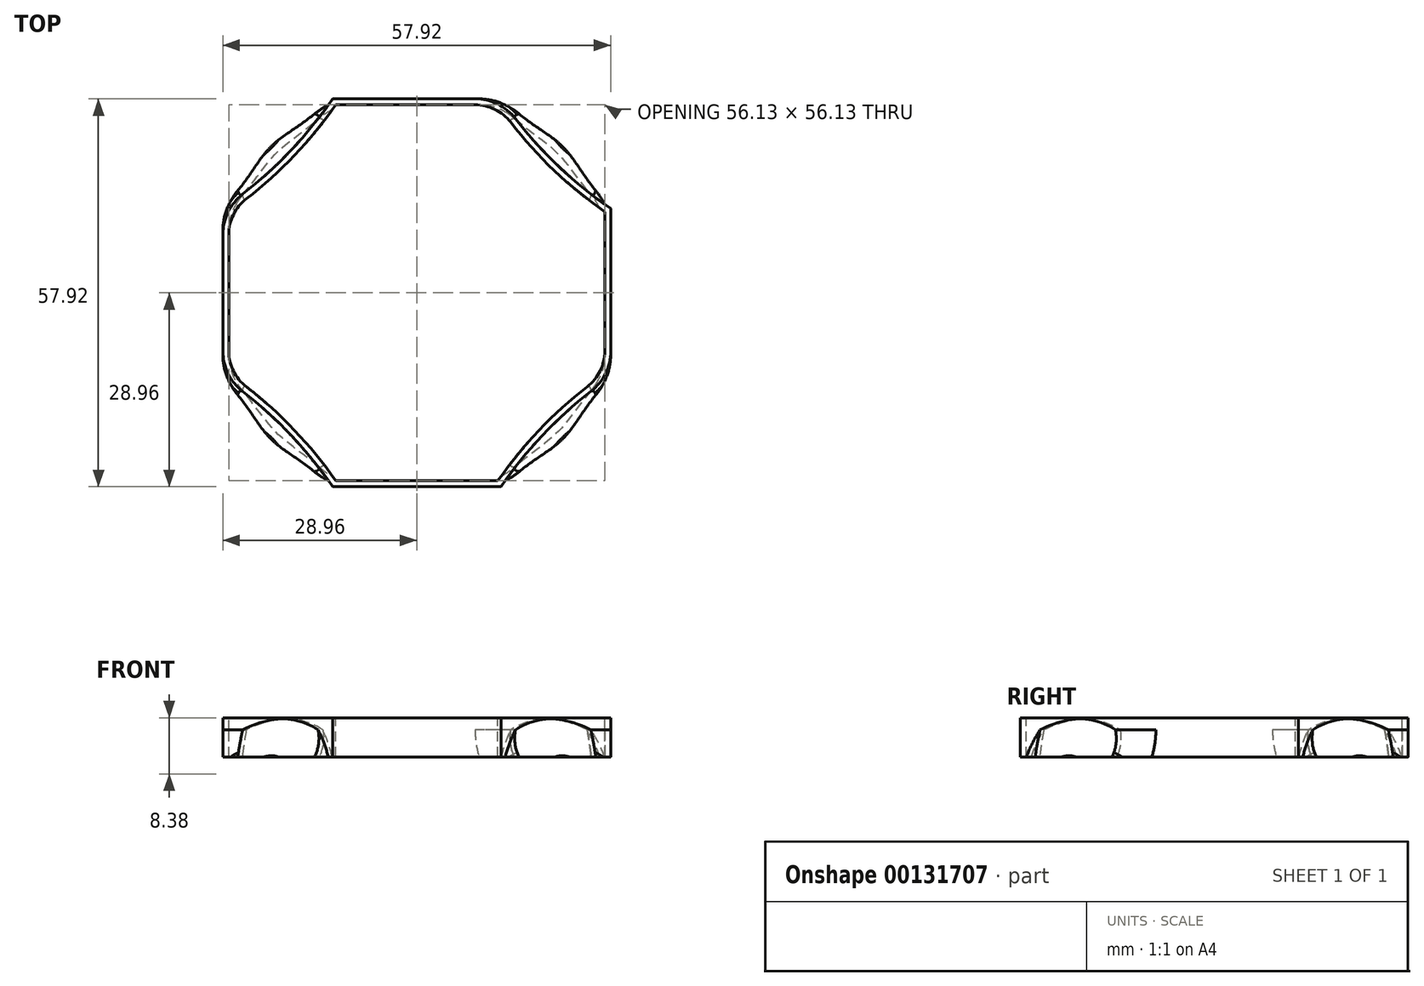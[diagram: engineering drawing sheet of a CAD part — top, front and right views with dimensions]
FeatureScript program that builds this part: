
annotation { "Feature Type Name" : "Feature", "Feature Type Description" : "" }
export const myFeature = defineFeature(function(context is Context, id is Id, definition is map)
    precondition{}
    {
        {
            var Q0;
            Q0=qCreatedBy(makeId("Top.planeOp"),FACE);
            var sketch = newSketch(context, id + "F0", { "sketchPlane" : qUnion([Q0])});
            skLineSegment(sketch, "E0.left", {"start": v(28.96, 12.57) * mm, "end": v(28.96, -12.57) * mm});
            skLineSegment(sketch, "E0.right", {"start": v(-28.96, 12.57) * mm, "end": v(-28.96, -12.57) * mm});
            skPoint(sketch, "E0.middle", {"position": v(0, 0) * mm});
            skLineSegment(sketch, "E1.bottom", {"start": v(12.57, 28.96) * mm, "end": v(-12.57, 28.96) * mm});
            skLineSegment(sketch, "E1.top", {"start": v(12.57, -28.96) * mm, "end": v(-12.57, -28.96) * mm});
            skArc(sketch, "E2", {"start": v(-28.96, 12.57) * mm, "mid": v(-20.01, 20.01) * mm, "end": v(-12.57, 28.96) * mm});
            skArc(sketch, "E3", {"start": v(12.57, 28.96) * mm, "mid": v(20.01, 20.01) * mm, "end": v(28.96, 12.57) * mm});
            skArc(sketch, "E4", {"start": v(28.96, -12.57) * mm, "mid": v(20.01, -20.01) * mm, "end": v(12.57, -28.96) * mm});
            skArc(sketch, "E5", {"start": v(-12.57, -28.96) * mm, "mid": v(-20.01, -20.01) * mm, "end": v(-28.96, -12.57) * mm});
            skSolve(sketch);
        }
        {
            var Q0;
            Q0=qCreatedBy(makeId("Top.planeOp"),FACE);
            cPlane(context, id + "F1", {"entities" : qUnion([Q0]), "cplaneType" : CPlaneType.OFFSET, "offset" : 14.02 * mm, "oppositeDirection" : true, "width" : 152.4 * mm, "height" : 152.4 * mm});
        }
        {
            var Q0;
            Q0=qCreatedBy(id+"F1.planeOp",FACE);
            var sketch = newSketch(context, id + "F2", { "sketchPlane" : qUnion([Q0])});
            skPoint(sketch, "E6.middle", {"position": v(0, 0) * mm});
            skArc(sketch, "E7", {"start": v(-37.14, -19.76) * mm, "mid": v(-28.96, 0) * mm, "end": v(-37.14, 19.76) * mm});
            skArc(sketch, "E8", {"start": v(-19.76, 37.14) * mm, "mid": v(0, 28.96) * mm, "end": v(19.76, 37.14) * mm});
            skArc(sketch, "E9", {"start": v(37.14, 19.76) * mm, "mid": v(28.96, 0) * mm, "end": v(37.14, -19.76) * mm});
            skArc(sketch, "E10", {"start": v(19.76, -37.14) * mm, "mid": v(0, -28.96) * mm, "end": v(-19.76, -37.14) * mm});
            skLineSegment(sketch, "E11", {"start": v(-44.09, 26.7) * mm, "end": v(-37.14, 19.76) * mm});
            skLineSegment(sketch, "E12", {"start": v(-19.76, 37.14) * mm, "end": v(-26.7, 44.09) * mm});
            skLineSegment(sketch, "E13", {"start": v(-26.7, 44.09) * mm, "end": v(-44.09, 26.7) * mm});
            skLineSegment(sketch, "E14", {"start": v(19.76, 37.14) * mm, "end": v(26.7, 44.09) * mm});
            skLineSegment(sketch, "E15", {"start": v(26.7, 44.09) * mm, "end": v(44.09, 26.7) * mm});
            skLineSegment(sketch, "E16", {"start": v(44.09, 26.7) * mm, "end": v(37.14, 19.76) * mm});
            skLineSegment(sketch, "E17", {"start": v(-19.76, -37.14) * mm, "end": v(-26.7, -44.09) * mm});
            skLineSegment(sketch, "E18", {"start": v(-26.7, -44.09) * mm, "end": v(-44.09, -26.7) * mm});
            skLineSegment(sketch, "E19", {"start": v(-44.09, -26.7) * mm, "end": v(-37.14, -19.76) * mm});
            skLineSegment(sketch, "E20", {"start": v(37.14, -19.76) * mm, "end": v(44.09, -26.7) * mm});
            skLineSegment(sketch, "E21", {"start": v(44.09, -26.7) * mm, "end": v(26.7, -44.09) * mm});
            skLineSegment(sketch, "E22", {"start": v(26.7, -44.09) * mm, "end": v(19.76, -37.14) * mm});
            skPoint(sketch, "E23.orphan", {"position": v(-29.11, 29.11) * mm});
            skPoint(sketch, "E24.orphan", {"position": v(29.1, 29.1) * mm});
            skPoint(sketch, "E25.orphan", {"position": v(29.11, -29.11) * mm});
            skPoint(sketch, "E26.orphan", {"position": v(-29.1, -29.1) * mm});
            skLineSegment(sketch, "E27.bottom", {"start": v(54.62, -53.7) * mm, "end": v(-54.62, -53.7) * mm});
            skLineSegment(sketch, "E27.top", {"start": v(54.62, 53.7) * mm, "end": v(-54.62, 53.7) * mm});
            skLineSegment(sketch, "E27.left", {"start": v(54.62, -53.7) * mm, "end": v(54.62, 53.7) * mm});
            skLineSegment(sketch, "E27.right", {"start": v(-54.62, -53.7) * mm, "end": v(-54.62, 53.7) * mm});
            skSolve(sketch);
        }
        {
            var Q0;
            Q0=makeQuery(id+"F0.imprint","IMPRINT",FACE,{"disambiguationData":[TD([[makeQuery(id+"F0.imprint","IMPRINT",EDGE,{"derivedFrom":sQuery(id+"F0.wireOp",EDGE,"E0.left")}),-1.0]])]});
            var Q1;
            Q1=qCreatedBy(id+"F1.planeOp",FACE);
            extrude(context, id + "F3", {"entities" : qUnion([Q0]), "endBound" : BoundingType.UP_TO_SURFACE, "oppositeDirection" : true, "endBoundEntityFace" : qUnion([Q1]), "depth" : 25.4 * mm});
        }
        {
            var Q0;
            Q0=makeQuery(id+"F0.imprint","IMPRINT",FACE,{"disambiguationData":[TD([[makeQuery(id+"F0.imprint","IMPRINT",EDGE,{"derivedFrom":sQuery(id+"F0.wireOp",EDGE,"E0.left")}),-1.0]])]});
            extrude(context, id + "F4", {"entities" : qUnion([Q0]), "operationType" : NewBodyOperationType.ADD, "depth" : 25.4 * mm});
        }
        {
            var Q0;
            Q0=qCreatedBy(id+"F1.planeOp",FACE);
            var sketch = newSketch(context, id + "F5", { "sketchPlane" : qUnion([Q0])});
            skLineSegment(sketch, "E28", {"start": v(-26.36, -26.36) * mm, "end": v(26.36, 26.36) * mm});
            skLineSegment(sketch, "E29", {"start": v(26.36, -26.36) * mm, "end": v(-26.36, 26.36) * mm});
            skSolve(sketch);
        }
        {
            var Q0;
            Q0=qCreatedBy(makeId("Front.planeOp"),FACE);
            var Q1;
            Q1=sQuery(id+"F5.wireOp",EDGE,"E28");
            cPlane(context, id + "F6", {"entities" : qUnion([Q0, Q1]), "cplaneType" : CPlaneType.LINE_ANGLE, "offset" : 25.4 * mm, "angle" : 0 * degree, "width" : 152.4 * mm, "height" : 152.4 * mm});
        }
        {
            var Q0;
            Q0=qCreatedBy(makeId("Front.planeOp"),FACE);
            var Q1;
            Q1=sQuery(id+"F5.wireOp",EDGE,"E29");
            cPlane(context, id + "F7", {"entities" : qUnion([Q0, Q1]), "cplaneType" : CPlaneType.LINE_ANGLE, "offset" : 25.4 * mm, "angle" : 0 * degree, "width" : 152.4 * mm, "height" : 152.4 * mm});
        }
        {
            var Q0;
            Q0=qCreatedBy(id+"F6.planeOp",FACE);
            var sketch = newSketch(context, id + "F8", { "sketchPlane" : qUnion([Q0])});
            skCircle(sketch, "E30", {"center": v(50.22, 20.65) * mm, "radius": 28.32 * mm});
            skLineSegment(sketch, "E31.bottom", {"start": v(50.22, 20.65) * mm, "end": v(12.75, 20.65) * mm});
            skLineSegment(sketch, "E31.top", {"start": v(50.22, -14.02) * mm, "end": v(12.75, -14.02) * mm});
            skLineSegment(sketch, "E31.left", {"start": v(50.22, 20.65) * mm, "end": v(50.22, -14.02) * mm});
            skLineSegment(sketch, "E31.right", {"start": v(12.75, 20.65) * mm, "end": v(12.75, -14.02) * mm});
            skCircle(sketch, "E32", {"center": v(-50.22, 20.65) * mm, "radius": 28.32 * mm});
            skLineSegment(sketch, "E33.bottom", {"start": v(-50.22, 20.65) * mm, "end": v(-12.75, 20.65) * mm});
            skLineSegment(sketch, "E33.top", {"start": v(-50.22, -14.02) * mm, "end": v(-12.75, -14.02) * mm});
            skLineSegment(sketch, "E33.left", {"start": v(-50.22, 20.65) * mm, "end": v(-50.22, -14.02) * mm});
            skLineSegment(sketch, "E33.right", {"start": v(-12.75, 20.65) * mm, "end": v(-12.75, -14.02) * mm});
            skSolve(sketch);
        }
        {
            var Q0;
            Q0=qCreatedBy(id+"F7.planeOp",FACE);
            var sketch = newSketch(context, id + "F9", { "sketchPlane" : qUnion([Q0])});
            skCircle(sketch, "E34", {"center": v(-50.22, 20.65) * mm, "radius": 28.32 * mm});
            skCircle(sketch, "E35", {"center": v(50.22, 20.65) * mm, "radius": 28.32 * mm});
            skLineSegment(sketch, "E36.bottom", {"start": v(-50.22, 20.65) * mm, "end": v(-12.75, 20.65) * mm});
            skLineSegment(sketch, "E36.top", {"start": v(-50.22, -14.02) * mm, "end": v(-12.75, -14.02) * mm});
            skLineSegment(sketch, "E36.left", {"start": v(-50.22, 20.65) * mm, "end": v(-50.22, -14.02) * mm});
            skLineSegment(sketch, "E36.right", {"start": v(-12.75, 20.65) * mm, "end": v(-12.75, -14.02) * mm});
            skLineSegment(sketch, "E37.bottom", {"start": v(50.22, 20.65) * mm, "end": v(12.75, 20.65) * mm});
            skLineSegment(sketch, "E37.top", {"start": v(50.22, -14.02) * mm, "end": v(12.75, -14.02) * mm});
            skLineSegment(sketch, "E37.left", {"start": v(50.22, 20.65) * mm, "end": v(50.22, -14.02) * mm});
            skLineSegment(sketch, "E37.right", {"start": v(12.75, 20.65) * mm, "end": v(12.75, -14.02) * mm});
            skSolve(sketch);
        }
        {
            var Q0;
            {var subQ1=sQuery(id+"F8.wireOp",EDGE,"E31.top");Q0=makeQuery(id+"F8.imprint","IMPRINT",FACE,{"disambiguationData":[TD([[makeQuery(id+"F8.imprint","IMPRINT",EDGE,{"derivedFrom":subQ1}),-1.0]])]});}
            var Q1;
            {var subQ1=sQuery(id+"F8.wireOp",EDGE,"E33.top");Q1=makeQuery(id+"F8.imprint","IMPRINT",FACE,{"disambiguationData":[TD([[makeQuery(id+"F8.imprint","IMPRINT",EDGE,{"derivedFrom":subQ1}),1.0]])]});}
            extrude(context, id + "F10", {"entities" : qUnion([Q0, Q1]), "operationType" : NewBodyOperationType.ADD, "endBound" : BoundingType.SYMMETRIC, "depth" : 38.1 * mm});
        }
        {
            var Q0;
            {var subQ1=sQuery(id+"F9.wireOp",EDGE,"E36.top");Q0=makeQuery(id+"F9.imprint","IMPRINT",FACE,{"disambiguationData":[TD([[makeQuery(id+"F9.imprint","IMPRINT",EDGE,{"derivedFrom":subQ1}),1.0]])]});}
            var Q1;
            {var subQ1=sQuery(id+"F9.wireOp",EDGE,"E37.top");Q1=makeQuery(id+"F9.imprint","IMPRINT",FACE,{"disambiguationData":[TD([[makeQuery(id+"F9.imprint","IMPRINT",EDGE,{"derivedFrom":subQ1}),-1.0]])]});}
            extrude(context, id + "F11", {"entities" : qUnion([Q0, Q1]), "operationType" : NewBodyOperationType.ADD, "endBound" : BoundingType.SYMMETRIC, "depth" : 38.1 * mm});
        }
        {
            var Q0;
            Q0=makeQuery(id+"F10.opExtrude","CAP_EDGE",EDGE,{"disambiguationData":[OSD([sQuery(id+"F8.wireOp",EDGE,"E30")])],"isStart":false});
            var Q1;
            Q1=makeQuery(id+"F10.opExtrude","CAP_EDGE",EDGE,{"disambiguationData":[OSD([sQuery(id+"F8.wireOp",EDGE,"E30")])],"isStart":true});
            var Q2;
            Q2=makeQuery(id+"F10.opExtrude","CAP_EDGE",EDGE,{"disambiguationData":[OSD([sQuery(id+"F8.wireOp",EDGE,"E32")])],"isStart":false});
            var Q3;
            Q3=makeQuery(id+"F10.opExtrude","CAP_EDGE",EDGE,{"disambiguationData":[OSD([sQuery(id+"F8.wireOp",EDGE,"E32")])],"isStart":true});
            var Q4;
            Q4=makeQuery(id+"F11.opExtrude","CAP_EDGE",EDGE,{"disambiguationData":[OSD([sQuery(id+"F9.wireOp",EDGE,"E35")])],"isStart":true});
            var Q5;
            Q5=makeQuery(id+"F11.opExtrude","CAP_EDGE",EDGE,{"disambiguationData":[OSD([sQuery(id+"F9.wireOp",EDGE,"E35")])],"isStart":false});
            var Q6;
            Q6=makeQuery(id+"F11.opExtrude","CAP_EDGE",EDGE,{"disambiguationData":[OSD([sQuery(id+"F9.wireOp",EDGE,"E34")])],"isStart":true});
            var Q7;
            Q7=makeQuery(id+"F11.opExtrude","CAP_EDGE",EDGE,{"disambiguationData":[OSD([sQuery(id+"F9.wireOp",EDGE,"E34")])],"isStart":false});
            fillet(context, id + "F12", {"entities" : qUnion([Q0, Q1, Q2, Q3, Q4, Q5, Q6, Q7]), "radius" : 19.05 * mm, "tangentPropagation" : true, "allowEdgeOverflow" : false});
        }
        {
            var Q0;
            Q0=makeQuery(id+"F2.imprint","IMPRINT",FACE,{"disambiguationData":[TD([[makeQuery(id+"F2.imprint","IMPRINT",EDGE,{"derivedFrom":sQuery(id+"F2.wireOp",EDGE,"E7")}),1.0]])]});
            extrude(context, id + "F13", {"entities" : qUnion([Q0]), "operationType" : NewBodyOperationType.REMOVE, "depth" : 50.8 * mm});
        }
        {
            var Q0;
            Q0=makeQuery(id+"F13.boolean.opBoolean","INTERSECT",EDGE,{"derivedFrom":[makeQuery(id+"F12.opFillet","BLEND_FACE",FACE,{"disambiguationData":[OSD([sQuery(id+"F8.wireOp",EDGE,"E30")])]}),makeQuery(id+"F13.opExtrude","SWEPT_FACE",FACE,{"disambiguationData":[OSD([sQuery(id+"F2.wireOp",EDGE,"E19")])]})]});
            var Q1;
            Q1=makeQuery(id+"F13.boolean.opBoolean","INTERSECT",EDGE,{"derivedFrom":[makeQuery(id+"F12.opFillet","BLEND_FACE",FACE,{"disambiguationData":[OSD([sQuery(id+"F8.wireOp",EDGE,"E30")])]}),makeQuery(id+"F13.opExtrude","SWEPT_FACE",FACE,{"disambiguationData":[OSD([sQuery(id+"F2.wireOp",EDGE,"E17")])]})]});
            var Q2;
            Q2=makeQuery(id+"F13.boolean.opBoolean","INTERSECT",EDGE,{"derivedFrom":[makeQuery(id+"F12.opFillet","BLEND_FACE",FACE,{"disambiguationData":[OSD([sQuery(id+"F8.wireOp",EDGE,"E32")])]}),makeQuery(id+"F13.opExtrude","SWEPT_FACE",FACE,{"disambiguationData":[OSD([sQuery(id+"F2.wireOp",EDGE,"E14")])]})]});
            var Q3;
            Q3=makeQuery(id+"F13.boolean.opBoolean","INTERSECT",EDGE,{"derivedFrom":[makeQuery(id+"F12.opFillet","BLEND_FACE",FACE,{"disambiguationData":[OSD([sQuery(id+"F8.wireOp",EDGE,"E32")])]}),makeQuery(id+"F13.opExtrude","SWEPT_FACE",FACE,{"disambiguationData":[OSD([sQuery(id+"F2.wireOp",EDGE,"E16")])]})]});
            var Q4;
            Q4=makeQuery(id+"F13.boolean.opBoolean","INTERSECT",EDGE,{"derivedFrom":[makeQuery(id+"F12.opFillet","BLEND_FACE",FACE,{"disambiguationData":[OSD([sQuery(id+"F9.wireOp",EDGE,"E35")])]}),makeQuery(id+"F13.opExtrude","SWEPT_FACE",FACE,{"disambiguationData":[OSD([sQuery(id+"F2.wireOp",EDGE,"E11")])]})]});
            var Q5;
            Q5=makeQuery(id+"F13.boolean.opBoolean","INTERSECT",EDGE,{"derivedFrom":[makeQuery(id+"F12.opFillet","BLEND_FACE",FACE,{"disambiguationData":[OSD([sQuery(id+"F9.wireOp",EDGE,"E35")])]}),makeQuery(id+"F13.opExtrude","SWEPT_FACE",FACE,{"disambiguationData":[OSD([sQuery(id+"F2.wireOp",EDGE,"E12")])]})]});
            var Q6;
            Q6=makeQuery(id+"F13.boolean.opBoolean","INTERSECT",EDGE,{"derivedFrom":[makeQuery(id+"F12.opFillet","BLEND_FACE",FACE,{"disambiguationData":[OSD([sQuery(id+"F9.wireOp",EDGE,"E34")])]}),makeQuery(id+"F13.opExtrude","SWEPT_FACE",FACE,{"disambiguationData":[OSD([sQuery(id+"F2.wireOp",EDGE,"E22")])]})]});
            var Q7;
            Q7=makeQuery(id+"F13.boolean.opBoolean","INTERSECT",EDGE,{"derivedFrom":[makeQuery(id+"F12.opFillet","BLEND_FACE",FACE,{"disambiguationData":[OSD([sQuery(id+"F9.wireOp",EDGE,"E34")])]}),makeQuery(id+"F13.opExtrude","SWEPT_FACE",FACE,{"disambiguationData":[OSD([sQuery(id+"F2.wireOp",EDGE,"E20")])]})]});
            fillet(context, id + "F14", {"entities" : qUnion([Q0, Q1, Q2, Q3, Q4, Q5, Q6, Q7]), "radius" : 5.6 * mm, "tangentPropagation" : true, "allowEdgeOverflow" : false});
        }
        {
            var Q0;
            {var subQ0=sQuery(id+"F0.wireOp",EDGE,"E5");Q0=makeQuery(id+"F12.opFillet","BLEND_EDGE",EDGE,{"blendedFrom":[makeQuery(id+"F10.opExtrude","CAP_EDGE",EDGE,{"disambiguationData":[OSD([sQuery(id+"F8.wireOp",EDGE,"E30")])],"isStart":false}),makeQuery(id+"F4.boolean.opBoolean","MERGE",FACE,{"derivedFrom":[makeQuery(id+"F3.opExtrude","SWEPT_FACE",FACE,{"disambiguationData":[OSD([subQ0])]}),makeQuery(id+"F4.opExtrude","SWEPT_FACE",FACE,{"disambiguationData":[OSD([subQ0])]})]})],"blendedInto":[makeQuery(id+"F4.boolean.opBoolean","MERGE",FACE,{"derivedFrom":[makeQuery(id+"F3.opExtrude","SWEPT_FACE",FACE,{"disambiguationData":[OSD([subQ0])]}),makeQuery(id+"F4.opExtrude","SWEPT_FACE",FACE,{"disambiguationData":[OSD([subQ0])]})]})]});}
            var Q1;
            {var subQ0=sQuery(id+"F0.wireOp",EDGE,"E0.right");Q1=makeQuery(id+"F12.opFillet","BLEND_EDGE",EDGE,{"blendedFrom":[makeQuery(id+"F10.opExtrude","CAP_EDGE",EDGE,{"disambiguationData":[OSD([sQuery(id+"F8.wireOp",EDGE,"E30")])],"isStart":false}),makeQuery(id+"F4.boolean.opBoolean","MERGE",FACE,{"derivedFrom":[makeQuery(id+"F3.opExtrude","SWEPT_FACE",FACE,{"disambiguationData":[OSD([subQ0])]}),makeQuery(id+"F4.opExtrude","SWEPT_FACE",FACE,{"disambiguationData":[OSD([subQ0])]})]})],"blendedInto":[makeQuery(id+"F4.boolean.opBoolean","MERGE",FACE,{"derivedFrom":[makeQuery(id+"F3.opExtrude","SWEPT_FACE",FACE,{"disambiguationData":[OSD([subQ0])]}),makeQuery(id+"F4.opExtrude","SWEPT_FACE",FACE,{"disambiguationData":[OSD([subQ0])]})]})]});}
            var Q2;
            {var subQ0=sQuery(id+"F0.wireOp",EDGE,"E1.top");Q2=makeQuery(id+"F12.opFillet","BLEND_EDGE",EDGE,{"blendedFrom":[makeQuery(id+"F10.opExtrude","CAP_EDGE",EDGE,{"disambiguationData":[OSD([sQuery(id+"F8.wireOp",EDGE,"E30")])],"isStart":true}),makeQuery(id+"F4.boolean.opBoolean","MERGE",FACE,{"derivedFrom":[makeQuery(id+"F3.opExtrude","SWEPT_FACE",FACE,{"disambiguationData":[OSD([subQ0])]}),makeQuery(id+"F4.opExtrude","SWEPT_FACE",FACE,{"disambiguationData":[OSD([subQ0])]})]})],"blendedInto":[makeQuery(id+"F4.boolean.opBoolean","MERGE",FACE,{"derivedFrom":[makeQuery(id+"F3.opExtrude","SWEPT_FACE",FACE,{"disambiguationData":[OSD([subQ0])]}),makeQuery(id+"F4.opExtrude","SWEPT_FACE",FACE,{"disambiguationData":[OSD([subQ0])]})]})]});}
            var Q3;
            {var subQ0=sQuery(id+"F0.wireOp",EDGE,"E1.bottom");Q3=makeQuery(id+"F12.opFillet","BLEND_EDGE",EDGE,{"blendedFrom":[makeQuery(id+"F10.opExtrude","CAP_EDGE",EDGE,{"disambiguationData":[OSD([sQuery(id+"F8.wireOp",EDGE,"E32")])],"isStart":false}),makeQuery(id+"F4.boolean.opBoolean","MERGE",FACE,{"derivedFrom":[makeQuery(id+"F3.opExtrude","SWEPT_FACE",FACE,{"disambiguationData":[OSD([subQ0])]}),makeQuery(id+"F4.opExtrude","SWEPT_FACE",FACE,{"disambiguationData":[OSD([subQ0])]})]})],"blendedInto":[makeQuery(id+"F4.boolean.opBoolean","MERGE",FACE,{"derivedFrom":[makeQuery(id+"F3.opExtrude","SWEPT_FACE",FACE,{"disambiguationData":[OSD([subQ0])]}),makeQuery(id+"F4.opExtrude","SWEPT_FACE",FACE,{"disambiguationData":[OSD([subQ0])]})]})]});}
            var Q4;
            {var subQ0=sQuery(id+"F0.wireOp",EDGE,"E3");Q4=makeQuery(id+"F12.opFillet","BLEND_EDGE",EDGE,{"blendedFrom":[makeQuery(id+"F10.opExtrude","CAP_EDGE",EDGE,{"disambiguationData":[OSD([sQuery(id+"F8.wireOp",EDGE,"E32")])],"isStart":false}),makeQuery(id+"F4.boolean.opBoolean","MERGE",FACE,{"derivedFrom":[makeQuery(id+"F3.opExtrude","SWEPT_FACE",FACE,{"disambiguationData":[OSD([subQ0])]}),makeQuery(id+"F4.opExtrude","SWEPT_FACE",FACE,{"disambiguationData":[OSD([subQ0])]})]})],"blendedInto":[makeQuery(id+"F4.boolean.opBoolean","MERGE",FACE,{"derivedFrom":[makeQuery(id+"F3.opExtrude","SWEPT_FACE",FACE,{"disambiguationData":[OSD([subQ0])]}),makeQuery(id+"F4.opExtrude","SWEPT_FACE",FACE,{"disambiguationData":[OSD([subQ0])]})]})]});}
            var Q5;
            {var subQ0=sQuery(id+"F0.wireOp",EDGE,"E0.left");Q5=makeQuery(id+"F12.opFillet","BLEND_EDGE",EDGE,{"blendedFrom":[makeQuery(id+"F10.opExtrude","CAP_EDGE",EDGE,{"disambiguationData":[OSD([sQuery(id+"F8.wireOp",EDGE,"E32")])],"isStart":true}),makeQuery(id+"F4.boolean.opBoolean","MERGE",FACE,{"derivedFrom":[makeQuery(id+"F3.opExtrude","SWEPT_FACE",FACE,{"disambiguationData":[OSD([subQ0])]}),makeQuery(id+"F4.opExtrude","SWEPT_FACE",FACE,{"disambiguationData":[OSD([subQ0])]})]})],"blendedInto":[makeQuery(id+"F4.boolean.opBoolean","MERGE",FACE,{"derivedFrom":[makeQuery(id+"F3.opExtrude","SWEPT_FACE",FACE,{"disambiguationData":[OSD([subQ0])]}),makeQuery(id+"F4.opExtrude","SWEPT_FACE",FACE,{"disambiguationData":[OSD([subQ0])]})]})]});}
            var Q6;
            {var subQ0=sQuery(id+"F0.wireOp",EDGE,"E0.right");Q6=makeQuery(id+"F12.opFillet","BLEND_EDGE",EDGE,{"blendedFrom":[makeQuery(id+"F11.opExtrude","CAP_EDGE",EDGE,{"disambiguationData":[OSD([sQuery(id+"F9.wireOp",EDGE,"E35")])],"isStart":true}),makeQuery(id+"F4.boolean.opBoolean","MERGE",FACE,{"derivedFrom":[makeQuery(id+"F3.opExtrude","SWEPT_FACE",FACE,{"disambiguationData":[OSD([subQ0])]}),makeQuery(id+"F4.opExtrude","SWEPT_FACE",FACE,{"disambiguationData":[OSD([subQ0])]})]})],"blendedInto":[makeQuery(id+"F4.boolean.opBoolean","MERGE",FACE,{"derivedFrom":[makeQuery(id+"F3.opExtrude","SWEPT_FACE",FACE,{"disambiguationData":[OSD([subQ0])]}),makeQuery(id+"F4.opExtrude","SWEPT_FACE",FACE,{"disambiguationData":[OSD([subQ0])]})]})]});}
            var Q7;
            {var subQ0=sQuery(id+"F0.wireOp",EDGE,"E2");Q7=makeQuery(id+"F12.opFillet","BLEND_EDGE",EDGE,{"blendedFrom":[makeQuery(id+"F11.opExtrude","CAP_EDGE",EDGE,{"disambiguationData":[OSD([sQuery(id+"F9.wireOp",EDGE,"E35")])],"isStart":true}),makeQuery(id+"F4.boolean.opBoolean","MERGE",FACE,{"derivedFrom":[makeQuery(id+"F3.opExtrude","SWEPT_FACE",FACE,{"disambiguationData":[OSD([subQ0])]}),makeQuery(id+"F4.opExtrude","SWEPT_FACE",FACE,{"disambiguationData":[OSD([subQ0])]})]})],"blendedInto":[makeQuery(id+"F4.boolean.opBoolean","MERGE",FACE,{"derivedFrom":[makeQuery(id+"F3.opExtrude","SWEPT_FACE",FACE,{"disambiguationData":[OSD([subQ0])]}),makeQuery(id+"F4.opExtrude","SWEPT_FACE",FACE,{"disambiguationData":[OSD([subQ0])]})]})]});}
            var Q8;
            {var subQ0=sQuery(id+"F0.wireOp",EDGE,"E1.bottom");Q8=makeQuery(id+"F12.opFillet","BLEND_EDGE",EDGE,{"blendedFrom":[makeQuery(id+"F11.opExtrude","CAP_EDGE",EDGE,{"disambiguationData":[OSD([sQuery(id+"F9.wireOp",EDGE,"E35")])],"isStart":false}),makeQuery(id+"F4.boolean.opBoolean","MERGE",FACE,{"derivedFrom":[makeQuery(id+"F3.opExtrude","SWEPT_FACE",FACE,{"disambiguationData":[OSD([subQ0])]}),makeQuery(id+"F4.opExtrude","SWEPT_FACE",FACE,{"disambiguationData":[OSD([subQ0])]})]})],"blendedInto":[makeQuery(id+"F4.boolean.opBoolean","MERGE",FACE,{"derivedFrom":[makeQuery(id+"F3.opExtrude","SWEPT_FACE",FACE,{"disambiguationData":[OSD([subQ0])]}),makeQuery(id+"F4.opExtrude","SWEPT_FACE",FACE,{"disambiguationData":[OSD([subQ0])]})]})]});}
            var Q9;
            {var subQ0=sQuery(id+"F0.wireOp",EDGE,"E0.left");Q9=makeQuery(id+"F12.opFillet","BLEND_EDGE",EDGE,{"blendedFrom":[makeQuery(id+"F11.opExtrude","CAP_EDGE",EDGE,{"disambiguationData":[OSD([sQuery(id+"F9.wireOp",EDGE,"E34")])],"isStart":false}),makeQuery(id+"F4.boolean.opBoolean","MERGE",FACE,{"derivedFrom":[makeQuery(id+"F3.opExtrude","SWEPT_FACE",FACE,{"disambiguationData":[OSD([subQ0])]}),makeQuery(id+"F4.opExtrude","SWEPT_FACE",FACE,{"disambiguationData":[OSD([subQ0])]})]})],"blendedInto":[makeQuery(id+"F4.boolean.opBoolean","MERGE",FACE,{"derivedFrom":[makeQuery(id+"F3.opExtrude","SWEPT_FACE",FACE,{"disambiguationData":[OSD([subQ0])]}),makeQuery(id+"F4.opExtrude","SWEPT_FACE",FACE,{"disambiguationData":[OSD([subQ0])]})]})]});}
            var Q10;
            {var subQ0=sQuery(id+"F0.wireOp",EDGE,"E4");Q10=makeQuery(id+"F12.opFillet","BLEND_EDGE",EDGE,{"blendedFrom":[makeQuery(id+"F11.opExtrude","CAP_EDGE",EDGE,{"disambiguationData":[OSD([sQuery(id+"F9.wireOp",EDGE,"E34")])],"isStart":false}),makeQuery(id+"F4.boolean.opBoolean","MERGE",FACE,{"derivedFrom":[makeQuery(id+"F3.opExtrude","SWEPT_FACE",FACE,{"disambiguationData":[OSD([subQ0])]}),makeQuery(id+"F4.opExtrude","SWEPT_FACE",FACE,{"disambiguationData":[OSD([subQ0])]})]})],"blendedInto":[makeQuery(id+"F4.boolean.opBoolean","MERGE",FACE,{"derivedFrom":[makeQuery(id+"F3.opExtrude","SWEPT_FACE",FACE,{"disambiguationData":[OSD([subQ0])]}),makeQuery(id+"F4.opExtrude","SWEPT_FACE",FACE,{"disambiguationData":[OSD([subQ0])]})]})]});}
            var Q11;
            {var subQ0=sQuery(id+"F0.wireOp",EDGE,"E1.top");Q11=makeQuery(id+"F12.opFillet","BLEND_EDGE",EDGE,{"blendedFrom":[makeQuery(id+"F11.opExtrude","CAP_EDGE",EDGE,{"disambiguationData":[OSD([sQuery(id+"F9.wireOp",EDGE,"E34")])],"isStart":true}),makeQuery(id+"F4.boolean.opBoolean","MERGE",FACE,{"derivedFrom":[makeQuery(id+"F3.opExtrude","SWEPT_FACE",FACE,{"disambiguationData":[OSD([subQ0])]}),makeQuery(id+"F4.opExtrude","SWEPT_FACE",FACE,{"disambiguationData":[OSD([subQ0])]})]})],"blendedInto":[makeQuery(id+"F4.boolean.opBoolean","MERGE",FACE,{"derivedFrom":[makeQuery(id+"F3.opExtrude","SWEPT_FACE",FACE,{"disambiguationData":[OSD([subQ0])]}),makeQuery(id+"F4.opExtrude","SWEPT_FACE",FACE,{"disambiguationData":[OSD([subQ0])]})]})]});}
            fillet(context, id + "F15", {"entities" : qUnion([Q0, Q1, Q2, Q3, Q4, Q5, Q6, Q7, Q8, Q9, Q10, Q11]), "radius" : 7.62 * mm, "tangentPropagation" : true, "allowEdgeOverflow" : false});
        }
        {
            var Q0;
            {var subQ0=sQuery(id+"F0.wireOp",EDGE,"E0.right");var subQ1=makeQuery(id+"F10.opExtrude","CAP_EDGE",EDGE,{"disambiguationData":[OSD([sQuery(id+"F8.wireOp",EDGE,"E30")])],"isStart":false});var subQ2=sQuery(id+"F0.wireOp",EDGE,"E5");Q0=makeQuery(id+"F15.opFillet","BLEND_EDGE",EDGE,{"blendedFrom":[makeQuery(id+"F12.opFillet","BLEND_EDGE",EDGE,{"blendedFrom":[subQ1,makeQuery(id+"F4.boolean.opBoolean","MERGE",FACE,{"derivedFrom":[makeQuery(id+"F3.opExtrude","SWEPT_FACE",FACE,{"disambiguationData":[OSD([subQ2])]}),makeQuery(id+"F4.opExtrude","SWEPT_FACE",FACE,{"disambiguationData":[OSD([subQ2])]})]})],"blendedInto":[makeQuery(id+"F4.boolean.opBoolean","MERGE",FACE,{"derivedFrom":[makeQuery(id+"F3.opExtrude","SWEPT_FACE",FACE,{"disambiguationData":[OSD([subQ2])]}),makeQuery(id+"F4.opExtrude","SWEPT_FACE",FACE,{"disambiguationData":[OSD([subQ2])]})]})]}),makeQuery(id+"F12.opFillet","BLEND_EDGE",EDGE,{"blendedFrom":[subQ1,makeQuery(id+"F4.boolean.opBoolean","MERGE",FACE,{"derivedFrom":[makeQuery(id+"F3.opExtrude","SWEPT_FACE",FACE,{"disambiguationData":[OSD([subQ0])]}),makeQuery(id+"F4.opExtrude","SWEPT_FACE",FACE,{"disambiguationData":[OSD([subQ0])]})]})],"blendedInto":[makeQuery(id+"F4.boolean.opBoolean","MERGE",FACE,{"derivedFrom":[makeQuery(id+"F3.opExtrude","SWEPT_FACE",FACE,{"disambiguationData":[OSD([subQ0])]}),makeQuery(id+"F4.opExtrude","SWEPT_FACE",FACE,{"disambiguationData":[OSD([subQ0])]})]})]})],"blendedInto":[]});}
            var Q1;
            {var subQ0=sQuery(id+"F0.wireOp",EDGE,"E1.top");var subQ1=makeQuery(id+"F10.opExtrude","CAP_EDGE",EDGE,{"disambiguationData":[OSD([sQuery(id+"F8.wireOp",EDGE,"E30")])],"isStart":true});var subQ2=sQuery(id+"F0.wireOp",EDGE,"E5");Q1=makeQuery(id+"F15.opFillet","BLEND_EDGE",EDGE,{"blendedFrom":[makeQuery(id+"F12.opFillet","BLEND_EDGE",EDGE,{"blendedFrom":[subQ1,makeQuery(id+"F4.boolean.opBoolean","MERGE",FACE,{"derivedFrom":[makeQuery(id+"F3.opExtrude","SWEPT_FACE",FACE,{"disambiguationData":[OSD([subQ2])]}),makeQuery(id+"F4.opExtrude","SWEPT_FACE",FACE,{"disambiguationData":[OSD([subQ2])]})]})],"blendedInto":[makeQuery(id+"F4.boolean.opBoolean","MERGE",FACE,{"derivedFrom":[makeQuery(id+"F3.opExtrude","SWEPT_FACE",FACE,{"disambiguationData":[OSD([subQ2])]}),makeQuery(id+"F4.opExtrude","SWEPT_FACE",FACE,{"disambiguationData":[OSD([subQ2])]})]})]}),makeQuery(id+"F12.opFillet","BLEND_EDGE",EDGE,{"blendedFrom":[subQ1,makeQuery(id+"F4.boolean.opBoolean","MERGE",FACE,{"derivedFrom":[makeQuery(id+"F3.opExtrude","SWEPT_FACE",FACE,{"disambiguationData":[OSD([subQ0])]}),makeQuery(id+"F4.opExtrude","SWEPT_FACE",FACE,{"disambiguationData":[OSD([subQ0])]})]})],"blendedInto":[makeQuery(id+"F4.boolean.opBoolean","MERGE",FACE,{"derivedFrom":[makeQuery(id+"F3.opExtrude","SWEPT_FACE",FACE,{"disambiguationData":[OSD([subQ0])]}),makeQuery(id+"F4.opExtrude","SWEPT_FACE",FACE,{"disambiguationData":[OSD([subQ0])]})]})]})],"blendedInto":[]});}
            var Q2;
            {var subQ0=sQuery(id+"F0.wireOp",EDGE,"E1.bottom");var subQ1=makeQuery(id+"F10.opExtrude","CAP_EDGE",EDGE,{"disambiguationData":[OSD([sQuery(id+"F8.wireOp",EDGE,"E32")])],"isStart":false});var subQ2=sQuery(id+"F0.wireOp",EDGE,"E3");Q2=makeQuery(id+"F15.opFillet","BLEND_EDGE",EDGE,{"blendedFrom":[makeQuery(id+"F12.opFillet","BLEND_EDGE",EDGE,{"blendedFrom":[subQ1,makeQuery(id+"F4.boolean.opBoolean","MERGE",FACE,{"derivedFrom":[makeQuery(id+"F3.opExtrude","SWEPT_FACE",FACE,{"disambiguationData":[OSD([subQ2])]}),makeQuery(id+"F4.opExtrude","SWEPT_FACE",FACE,{"disambiguationData":[OSD([subQ2])]})]})],"blendedInto":[makeQuery(id+"F4.boolean.opBoolean","MERGE",FACE,{"derivedFrom":[makeQuery(id+"F3.opExtrude","SWEPT_FACE",FACE,{"disambiguationData":[OSD([subQ2])]}),makeQuery(id+"F4.opExtrude","SWEPT_FACE",FACE,{"disambiguationData":[OSD([subQ2])]})]})]}),makeQuery(id+"F12.opFillet","BLEND_EDGE",EDGE,{"blendedFrom":[subQ1,makeQuery(id+"F4.boolean.opBoolean","MERGE",FACE,{"derivedFrom":[makeQuery(id+"F3.opExtrude","SWEPT_FACE",FACE,{"disambiguationData":[OSD([subQ0])]}),makeQuery(id+"F4.opExtrude","SWEPT_FACE",FACE,{"disambiguationData":[OSD([subQ0])]})]})],"blendedInto":[makeQuery(id+"F4.boolean.opBoolean","MERGE",FACE,{"derivedFrom":[makeQuery(id+"F3.opExtrude","SWEPT_FACE",FACE,{"disambiguationData":[OSD([subQ0])]}),makeQuery(id+"F4.opExtrude","SWEPT_FACE",FACE,{"disambiguationData":[OSD([subQ0])]})]})]})],"blendedInto":[]});}
            var Q3;
            {var subQ0=sQuery(id+"F0.wireOp",EDGE,"E0.left");var subQ1=makeQuery(id+"F10.opExtrude","CAP_EDGE",EDGE,{"disambiguationData":[OSD([sQuery(id+"F8.wireOp",EDGE,"E32")])],"isStart":true});var subQ2=sQuery(id+"F0.wireOp",EDGE,"E3");Q3=makeQuery(id+"F15.opFillet","BLEND_EDGE",EDGE,{"blendedFrom":[makeQuery(id+"F12.opFillet","BLEND_EDGE",EDGE,{"blendedFrom":[subQ1,makeQuery(id+"F4.boolean.opBoolean","MERGE",FACE,{"derivedFrom":[makeQuery(id+"F3.opExtrude","SWEPT_FACE",FACE,{"disambiguationData":[OSD([subQ2])]}),makeQuery(id+"F4.opExtrude","SWEPT_FACE",FACE,{"disambiguationData":[OSD([subQ2])]})]})],"blendedInto":[makeQuery(id+"F4.boolean.opBoolean","MERGE",FACE,{"derivedFrom":[makeQuery(id+"F3.opExtrude","SWEPT_FACE",FACE,{"disambiguationData":[OSD([subQ2])]}),makeQuery(id+"F4.opExtrude","SWEPT_FACE",FACE,{"disambiguationData":[OSD([subQ2])]})]})]}),makeQuery(id+"F12.opFillet","BLEND_EDGE",EDGE,{"blendedFrom":[subQ1,makeQuery(id+"F4.boolean.opBoolean","MERGE",FACE,{"derivedFrom":[makeQuery(id+"F3.opExtrude","SWEPT_FACE",FACE,{"disambiguationData":[OSD([subQ0])]}),makeQuery(id+"F4.opExtrude","SWEPT_FACE",FACE,{"disambiguationData":[OSD([subQ0])]})]})],"blendedInto":[makeQuery(id+"F4.boolean.opBoolean","MERGE",FACE,{"derivedFrom":[makeQuery(id+"F3.opExtrude","SWEPT_FACE",FACE,{"disambiguationData":[OSD([subQ0])]}),makeQuery(id+"F4.opExtrude","SWEPT_FACE",FACE,{"disambiguationData":[OSD([subQ0])]})]})]})],"blendedInto":[]});}
            var Q4;
            {var subQ0=sQuery(id+"F0.wireOp",EDGE,"E0.right");var subQ1=makeQuery(id+"F11.opExtrude","CAP_EDGE",EDGE,{"disambiguationData":[OSD([sQuery(id+"F9.wireOp",EDGE,"E35")])],"isStart":true});var subQ2=sQuery(id+"F0.wireOp",EDGE,"E2");Q4=makeQuery(id+"F15.opFillet","BLEND_EDGE",EDGE,{"blendedFrom":[makeQuery(id+"F12.opFillet","BLEND_EDGE",EDGE,{"blendedFrom":[subQ1,makeQuery(id+"F4.boolean.opBoolean","MERGE",FACE,{"derivedFrom":[makeQuery(id+"F3.opExtrude","SWEPT_FACE",FACE,{"disambiguationData":[OSD([subQ2])]}),makeQuery(id+"F4.opExtrude","SWEPT_FACE",FACE,{"disambiguationData":[OSD([subQ2])]})]})],"blendedInto":[makeQuery(id+"F4.boolean.opBoolean","MERGE",FACE,{"derivedFrom":[makeQuery(id+"F3.opExtrude","SWEPT_FACE",FACE,{"disambiguationData":[OSD([subQ2])]}),makeQuery(id+"F4.opExtrude","SWEPT_FACE",FACE,{"disambiguationData":[OSD([subQ2])]})]})]}),makeQuery(id+"F12.opFillet","BLEND_EDGE",EDGE,{"blendedFrom":[subQ1,makeQuery(id+"F4.boolean.opBoolean","MERGE",FACE,{"derivedFrom":[makeQuery(id+"F3.opExtrude","SWEPT_FACE",FACE,{"disambiguationData":[OSD([subQ0])]}),makeQuery(id+"F4.opExtrude","SWEPT_FACE",FACE,{"disambiguationData":[OSD([subQ0])]})]})],"blendedInto":[makeQuery(id+"F4.boolean.opBoolean","MERGE",FACE,{"derivedFrom":[makeQuery(id+"F3.opExtrude","SWEPT_FACE",FACE,{"disambiguationData":[OSD([subQ0])]}),makeQuery(id+"F4.opExtrude","SWEPT_FACE",FACE,{"disambiguationData":[OSD([subQ0])]})]})]})],"blendedInto":[]});}
            var Q5;
            {var subQ0=sQuery(id+"F0.wireOp",EDGE,"E1.bottom");var subQ1=makeQuery(id+"F11.opExtrude","CAP_EDGE",EDGE,{"disambiguationData":[OSD([sQuery(id+"F9.wireOp",EDGE,"E35")])],"isStart":false});var subQ2=sQuery(id+"F0.wireOp",EDGE,"E2");Q5=makeQuery(id+"F15.opFillet","BLEND_EDGE",EDGE,{"blendedFrom":[makeQuery(id+"F12.opFillet","BLEND_EDGE",EDGE,{"blendedFrom":[subQ1,makeQuery(id+"F4.boolean.opBoolean","MERGE",FACE,{"derivedFrom":[makeQuery(id+"F3.opExtrude","SWEPT_FACE",FACE,{"disambiguationData":[OSD([subQ2])]}),makeQuery(id+"F4.opExtrude","SWEPT_FACE",FACE,{"disambiguationData":[OSD([subQ2])]})]})],"blendedInto":[makeQuery(id+"F4.boolean.opBoolean","MERGE",FACE,{"derivedFrom":[makeQuery(id+"F3.opExtrude","SWEPT_FACE",FACE,{"disambiguationData":[OSD([subQ2])]}),makeQuery(id+"F4.opExtrude","SWEPT_FACE",FACE,{"disambiguationData":[OSD([subQ2])]})]})]}),makeQuery(id+"F12.opFillet","BLEND_EDGE",EDGE,{"blendedFrom":[subQ1,makeQuery(id+"F4.boolean.opBoolean","MERGE",FACE,{"derivedFrom":[makeQuery(id+"F3.opExtrude","SWEPT_FACE",FACE,{"disambiguationData":[OSD([subQ0])]}),makeQuery(id+"F4.opExtrude","SWEPT_FACE",FACE,{"disambiguationData":[OSD([subQ0])]})]})],"blendedInto":[makeQuery(id+"F4.boolean.opBoolean","MERGE",FACE,{"derivedFrom":[makeQuery(id+"F3.opExtrude","SWEPT_FACE",FACE,{"disambiguationData":[OSD([subQ0])]}),makeQuery(id+"F4.opExtrude","SWEPT_FACE",FACE,{"disambiguationData":[OSD([subQ0])]})]})]})],"blendedInto":[]});}
            var Q6;
            {var subQ0=sQuery(id+"F0.wireOp",EDGE,"E0.left");var subQ1=makeQuery(id+"F11.opExtrude","CAP_EDGE",EDGE,{"disambiguationData":[OSD([sQuery(id+"F9.wireOp",EDGE,"E34")])],"isStart":false});var subQ2=sQuery(id+"F0.wireOp",EDGE,"E4");Q6=makeQuery(id+"F15.opFillet","BLEND_EDGE",EDGE,{"blendedFrom":[makeQuery(id+"F12.opFillet","BLEND_EDGE",EDGE,{"blendedFrom":[subQ1,makeQuery(id+"F4.boolean.opBoolean","MERGE",FACE,{"derivedFrom":[makeQuery(id+"F3.opExtrude","SWEPT_FACE",FACE,{"disambiguationData":[OSD([subQ2])]}),makeQuery(id+"F4.opExtrude","SWEPT_FACE",FACE,{"disambiguationData":[OSD([subQ2])]})]})],"blendedInto":[makeQuery(id+"F4.boolean.opBoolean","MERGE",FACE,{"derivedFrom":[makeQuery(id+"F3.opExtrude","SWEPT_FACE",FACE,{"disambiguationData":[OSD([subQ2])]}),makeQuery(id+"F4.opExtrude","SWEPT_FACE",FACE,{"disambiguationData":[OSD([subQ2])]})]})]}),makeQuery(id+"F12.opFillet","BLEND_EDGE",EDGE,{"blendedFrom":[subQ1,makeQuery(id+"F4.boolean.opBoolean","MERGE",FACE,{"derivedFrom":[makeQuery(id+"F3.opExtrude","SWEPT_FACE",FACE,{"disambiguationData":[OSD([subQ0])]}),makeQuery(id+"F4.opExtrude","SWEPT_FACE",FACE,{"disambiguationData":[OSD([subQ0])]})]})],"blendedInto":[makeQuery(id+"F4.boolean.opBoolean","MERGE",FACE,{"derivedFrom":[makeQuery(id+"F3.opExtrude","SWEPT_FACE",FACE,{"disambiguationData":[OSD([subQ0])]}),makeQuery(id+"F4.opExtrude","SWEPT_FACE",FACE,{"disambiguationData":[OSD([subQ0])]})]})]})],"blendedInto":[]});}
            var Q7;
            {var subQ0=sQuery(id+"F0.wireOp",EDGE,"E1.top");var subQ1=makeQuery(id+"F11.opExtrude","CAP_EDGE",EDGE,{"disambiguationData":[OSD([sQuery(id+"F9.wireOp",EDGE,"E34")])],"isStart":true});var subQ2=sQuery(id+"F0.wireOp",EDGE,"E4");Q7=makeQuery(id+"F15.opFillet","BLEND_EDGE",EDGE,{"blendedFrom":[makeQuery(id+"F12.opFillet","BLEND_EDGE",EDGE,{"blendedFrom":[subQ1,makeQuery(id+"F4.boolean.opBoolean","MERGE",FACE,{"derivedFrom":[makeQuery(id+"F3.opExtrude","SWEPT_FACE",FACE,{"disambiguationData":[OSD([subQ2])]}),makeQuery(id+"F4.opExtrude","SWEPT_FACE",FACE,{"disambiguationData":[OSD([subQ2])]})]})],"blendedInto":[makeQuery(id+"F4.boolean.opBoolean","MERGE",FACE,{"derivedFrom":[makeQuery(id+"F3.opExtrude","SWEPT_FACE",FACE,{"disambiguationData":[OSD([subQ2])]}),makeQuery(id+"F4.opExtrude","SWEPT_FACE",FACE,{"disambiguationData":[OSD([subQ2])]})]})]}),makeQuery(id+"F12.opFillet","BLEND_EDGE",EDGE,{"blendedFrom":[subQ1,makeQuery(id+"F4.boolean.opBoolean","MERGE",FACE,{"derivedFrom":[makeQuery(id+"F3.opExtrude","SWEPT_FACE",FACE,{"disambiguationData":[OSD([subQ0])]}),makeQuery(id+"F4.opExtrude","SWEPT_FACE",FACE,{"disambiguationData":[OSD([subQ0])]})]})],"blendedInto":[makeQuery(id+"F4.boolean.opBoolean","MERGE",FACE,{"derivedFrom":[makeQuery(id+"F3.opExtrude","SWEPT_FACE",FACE,{"disambiguationData":[OSD([subQ0])]}),makeQuery(id+"F4.opExtrude","SWEPT_FACE",FACE,{"disambiguationData":[OSD([subQ0])]})]})]})],"blendedInto":[]});}
            fillet(context, id + "F16", {"entities" : qUnion([Q0, Q1, Q2, Q3, Q4, Q5, Q6, Q7]), "radius" : 7.62 * mm, "tangentPropagation" : true, "allowEdgeOverflow" : false});
        }
        {
            var Q0;
            Q0=makeQuery(id+"F11.boolean.opBoolean","MERGE",FACE,{"derivedFrom":[makeQuery(id+"F10.boolean.opBoolean","MERGE",FACE,{"derivedFrom":[makeQuery(id+"F3.opExtrude","CAP_FACE",FACE,{"disambiguationData":[OSD([dummyQuery(id+"F1.planeOp",FACE)])],"isStart":false}),makeQuery(id+"F10.opExtrude","SWEPT_FACE",FACE,{"disambiguationData":[OSD([sQuery(id+"F8.wireOp",EDGE,"E31.top")])]}),makeQuery(id+"F10.opExtrude","SWEPT_FACE",FACE,{"disambiguationData":[OSD([sQuery(id+"F8.wireOp",EDGE,"E33.top")])]})]}),makeQuery(id+"F11.opExtrude","SWEPT_FACE",FACE,{"disambiguationData":[OSD([sQuery(id+"F9.wireOp",EDGE,"E36.top")])]}),makeQuery(id+"F11.opExtrude","SWEPT_FACE",FACE,{"disambiguationData":[OSD([sQuery(id+"F9.wireOp",EDGE,"E37.top")])]})]});
            shell(context, id + "F17", {"entities" : qUnion([Q0]), "thickness" : 0.89 * mm});
        }
        {
            var Q0;
            Q0=qCreatedBy(makeId("Front.planeOp"),FACE);
            var sketch = newSketch(context, id + "F18", { "sketchPlane" : qUnion([Q0])});
            skLineSegment(sketch, "E38.bottom", {"start": v(-49.75, 0) * mm, "end": v(49.75, 0) * mm});
            skLineSegment(sketch, "E38.top", {"start": v(-49.75, -19.7) * mm, "end": v(49.75, -19.7) * mm});
            skLineSegment(sketch, "E38.left", {"start": v(-49.75, -19.7) * mm, "end": v(-49.75, 0) * mm});
            skLineSegment(sketch, "E38.right", {"start": v(49.75, -19.7) * mm, "end": v(49.75, 0) * mm});
            skPoint(sketch, "E38.middle", {"position": v(0, -9.85) * mm});
            skLineSegment(sketch, "E39.bottom", {"start": v(49.75, 5.84) * mm, "end": v(-49.75, 5.84) * mm});
            skLineSegment(sketch, "E39.top", {"start": v(49.75, 30.08) * mm, "end": v(-49.75, 30.08) * mm});
            skLineSegment(sketch, "E39.left", {"start": v(49.75, 5.84) * mm, "end": v(49.75, 30.08) * mm});
            skLineSegment(sketch, "E39.right", {"start": v(-49.75, 5.84) * mm, "end": v(-49.75, 30.08) * mm});
            skPoint(sketch, "E39.middle", {"position": v(0, 17.96) * mm});
            skSolve(sketch);
        }
        {
            var Q0;
            Q0=qSketchRegion(id+"F18",true);
            extrude(context, id + "F19", {"entities" : qUnion([Q0]), "operationType" : NewBodyOperationType.REMOVE, "endBound" : BoundingType.SYMMETRIC, "oppositeDirection" : true, "depth" : 92.96 * mm});
        }
    });
